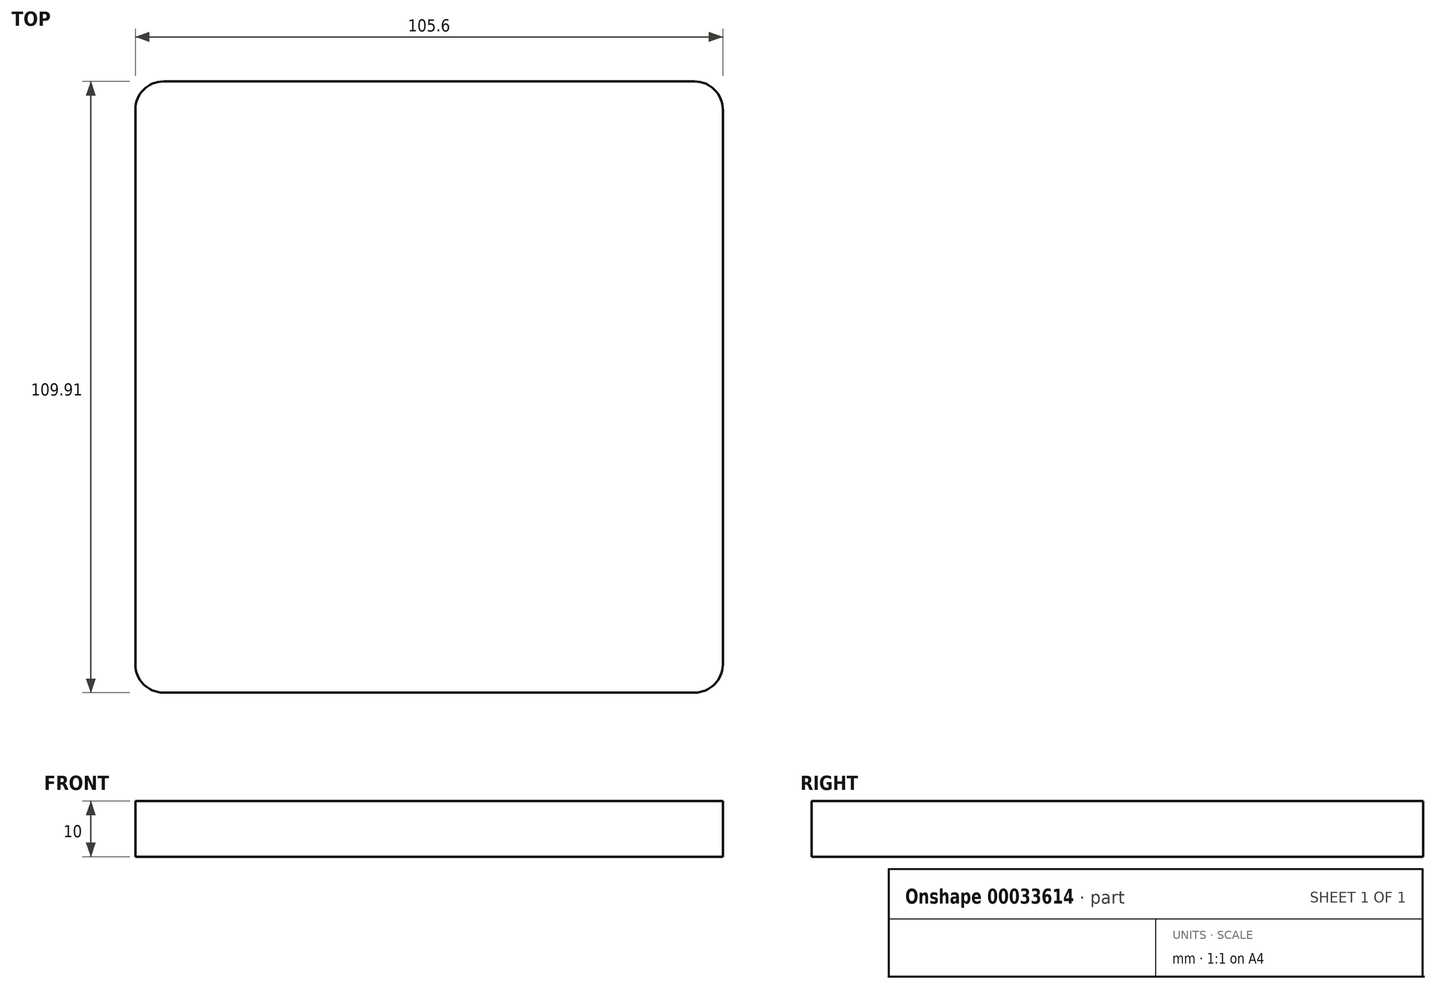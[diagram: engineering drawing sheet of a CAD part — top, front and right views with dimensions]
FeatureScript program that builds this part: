
annotation { "Feature Type Name" : "Feature", "Feature Type Description" : "" }
export const myFeature = defineFeature(function(context is Context, id is Id, definition is map)
    precondition{}
    {
        {
            var Q0;
            Q0=qCreatedBy(makeId("Top.planeOp"),FACE);
            var sketch = newSketch(context, id + "F0", { "sketchPlane" : qUnion([Q0])});
            skLineSegment(sketch, "E0.bottom", {"start": v(-58.17, -56.57) * mm, "end": v(47.43, -56.57) * mm});
            skLineSegment(sketch, "E0.top", {"start": v(-58.17, 53.34) * mm, "end": v(47.43, 53.34) * mm});
            skLineSegment(sketch, "E0.left", {"start": v(-58.17, -56.57) * mm, "end": v(-58.17, 53.34) * mm});
            skLineSegment(sketch, "E0.right", {"start": v(47.43, -56.57) * mm, "end": v(47.43, 53.34) * mm});
            skSolve(sketch);
        }
        {
            var Q0;
            Q0=sQuery(id+"F0.wireOp",EDGE,"E0.top");
            var Q1;
            Q1=sQuery(id+"F0.wireOp",EDGE,"E0.left");
            var Q2;
            Q2=sQuery(id+"F0.wireOp",EDGE,"E0.bottom");
            var Q3;
            Q3=sQuery(id+"F0.wireOp",EDGE,"E0.right");
            extrude(context, id + "F1", {"bodyType" : ToolBodyType.SURFACE, "surfaceEntities" : qUnion([Q0, Q1, Q2, Q3]), "depth" : 10 * mm});
        }
        {
            var Q0;
            Q0=makeQuery(id+"F1.opExtrude","SWEPT_FACE",FACE,{"disambiguationData":[OSD([sQuery(id+"F0.wireOp",EDGE,"E0.right")])]});
            var Q1;
            Q1=makeQuery(id+"F1.opExtrude","SWEPT_FACE",FACE,{"disambiguationData":[OSD([sQuery(id+"F0.wireOp",EDGE,"E0.bottom")])]});
            var Q2;
            Q2=makeQuery(id+"F1.opExtrude","SWEPT_FACE",FACE,{"disambiguationData":[OSD([sQuery(id+"F0.wireOp",EDGE,"E0.left")])]});
            var Q3;
            Q3=makeQuery(id+"F1.opExtrude","SWEPT_FACE",FACE,{"disambiguationData":[OSD([sQuery(id+"F0.wireOp",EDGE,"E0.top")])]});
            var Q4;
            Q4=makeQuery(id+"F1.opExtrude","SWEPT_EDGE",EDGE,{"disambiguationData":[OSD([sQuery(id+"F0.wireOp",VERTEX,"E0.bottom.start")])]});
            var Q5;
            Q5=makeQuery(id+"F1.opExtrude","SWEPT_EDGE",EDGE,{"disambiguationData":[OSD([sQuery(id+"F0.wireOp",VERTEX,"E0.right.start")])]});
            var Q6;
            Q6=makeQuery(id+"F1.opExtrude","SWEPT_EDGE",EDGE,{"disambiguationData":[OSD([sQuery(id+"F0.wireOp",VERTEX,"E0.right.end")])]});
            var Q7;
            Q7=makeQuery(id+"F1.opExtrude","SWEPT_EDGE",EDGE,{"disambiguationData":[OSD([sQuery(id+"F0.wireOp",VERTEX,"E0.left.end")])]});
            fillet(context, id + "F2", {"entities" : qUnion([Q0, Q1, Q2, Q3, Q4, Q5, Q6, Q7]), "radius" : 5.08 * mm, "tangentPropagation" : true, "allowEdgeOverflow" : false});
        }
    });
